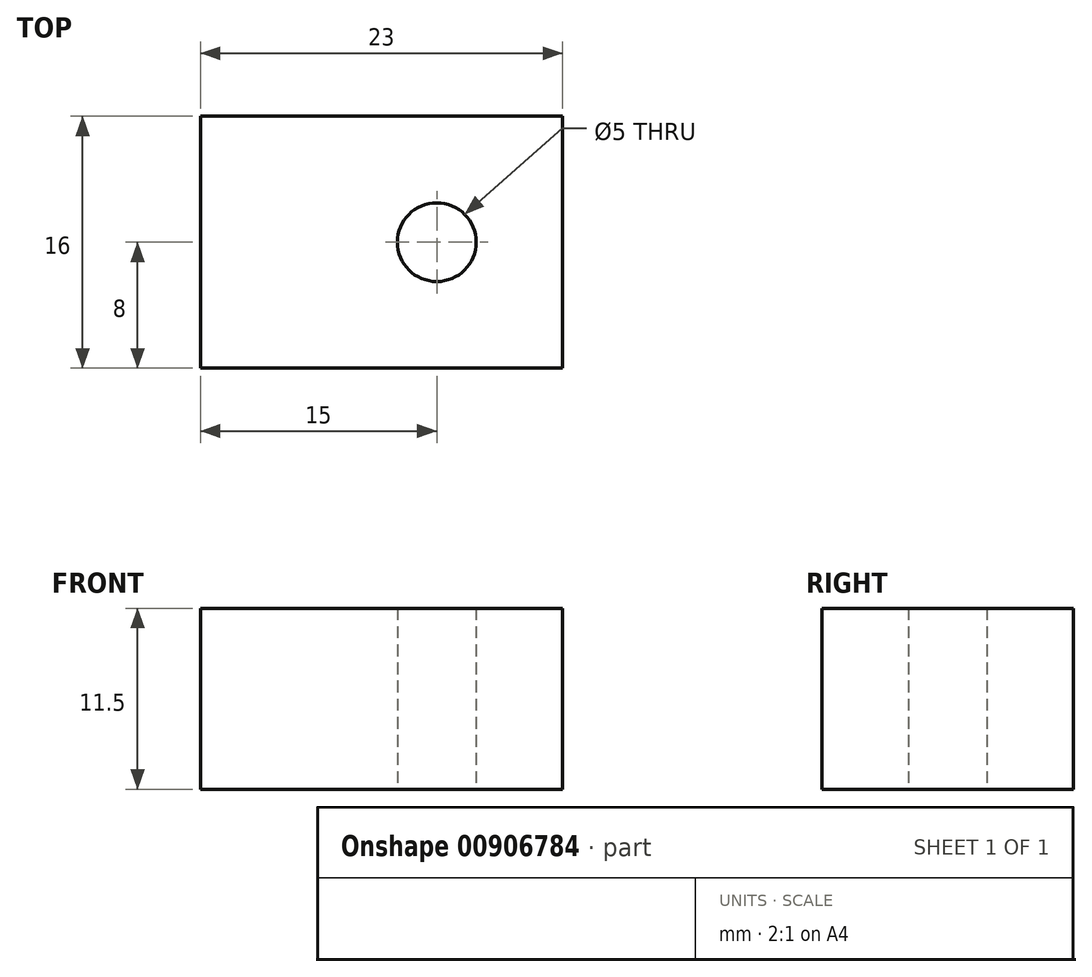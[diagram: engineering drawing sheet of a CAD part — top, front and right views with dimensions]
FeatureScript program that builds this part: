
annotation { "Feature Type Name" : "Feature", "Feature Type Description" : "" }
export const myFeature = defineFeature(function(context is Context, id is Id, definition is map)
    precondition{}
    {
        {
            var Q0;
            Q0=qCreatedBy(makeId("Top.planeOp"),FACE);
            var sketch = newSketch(context, id + "F0", { "sketchPlane" : qUnion([Q0])});
            skLineSegment(sketch, "E0.bottom", {"start": v(-11.5, 8) * mm, "end": v(11.5, 8) * mm});
            skLineSegment(sketch, "E0.top", {"start": v(-11.5, -8) * mm, "end": v(11.5, -8) * mm});
            skLineSegment(sketch, "E0.left", {"start": v(-11.5, 8) * mm, "end": v(-11.5, -8) * mm});
            skLineSegment(sketch, "E0.right", {"start": v(11.5, 8) * mm, "end": v(11.5, -8) * mm});
            skPoint(sketch, "E0.middle", {"position": v(0, 0) * mm});
            skCircle(sketch, "E1", {"center": v(3.5, 0) * mm, "radius": 2.5 * mm});
            skSolve(sketch);
        }
        {
            var Q0;
            Q0=makeQuery(id+"F0.imprint","IMPRINT",FACE,{"disambiguationData":[TD([[makeQuery(id+"F0.imprint","IMPRINT",EDGE,{"derivedFrom":sQuery(id+"F0.wireOp",EDGE,"E0.bottom")}),-1.0]])]});
            extrude(context, id + "F1", {"entities" : qUnion([Q0]), "depth" : 11.5 * mm, "offsetDistance" : 25 * mm});
        }
    });
